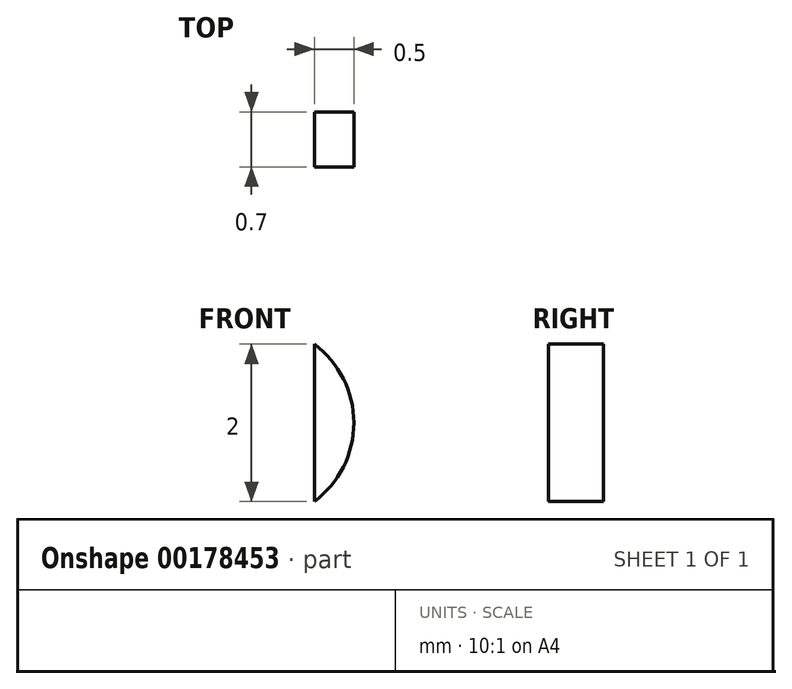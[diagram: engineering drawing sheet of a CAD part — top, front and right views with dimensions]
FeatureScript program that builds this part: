
annotation { "Feature Type Name" : "Feature", "Feature Type Description" : "" }
export const myFeature = defineFeature(function(context is Context, id is Id, definition is map)
    precondition{}
    {
        {
            var Q0;
            Q0=qCreatedBy(makeId("Front.planeOp"),FACE);
            var sketch = newSketch(context, id + "F0", { "sketchPlane" : qUnion([Q0])});
            skArc(sketch, "E0", {"start": v(0.75, -1) * mm, "mid": v(1.25, 0) * mm, "end": v(0.75, 1) * mm});
            skLineSegment(sketch, "E1", {"start": v(0.75, 1) * mm, "end": v(0.75, -1) * mm});
            skSolve(sketch);
        }
        {
            var Q0;
            Q0 = qSketchRegion(id + "F0", true);
            extrude(context, id + "F1", {"entities" : qUnion([Q0]), "depth" : 0.7 * mm});
        }
    });
